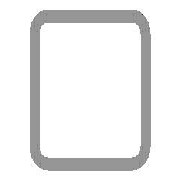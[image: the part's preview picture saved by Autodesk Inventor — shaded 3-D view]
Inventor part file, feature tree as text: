
AUTODESK INVENTOR PART (.ipt)
format: ipt  version: 2025 (Build 290162010, 162A)  size: 133,120 bytes
history: native  units: mm (DEFAULTED — no unit token found)
features: other x4, sketch x1, plane x1
ambient origin geometry x8: Origin, YZ Plane, XZ Plane, XY Plane, X Axis, Y Axis, Z Axis, Center Point
bodies: Solid1 (feature_tree), Body (feature_tree)
feature tree (6):
  parser-record x1  (decoder bookkeeping rows leaked as tree rows — omitted from the tree; the rows remain in map.json)
  other  "Driven Length"
  other  "Start Plane"
  other  "End Plane"
  sketch  "Sketch3"  dims[d3=2906.0mm d4=0.0mm d7=4.0mm d9=40.0mm d11=40.0mm d12=2.0mm d13=-0.0mm d14=2906.0mm d15=20.0mm d16=20.0mm d17=90.0deg d18=2906.0mm]
  plane  "Work Plane3"
